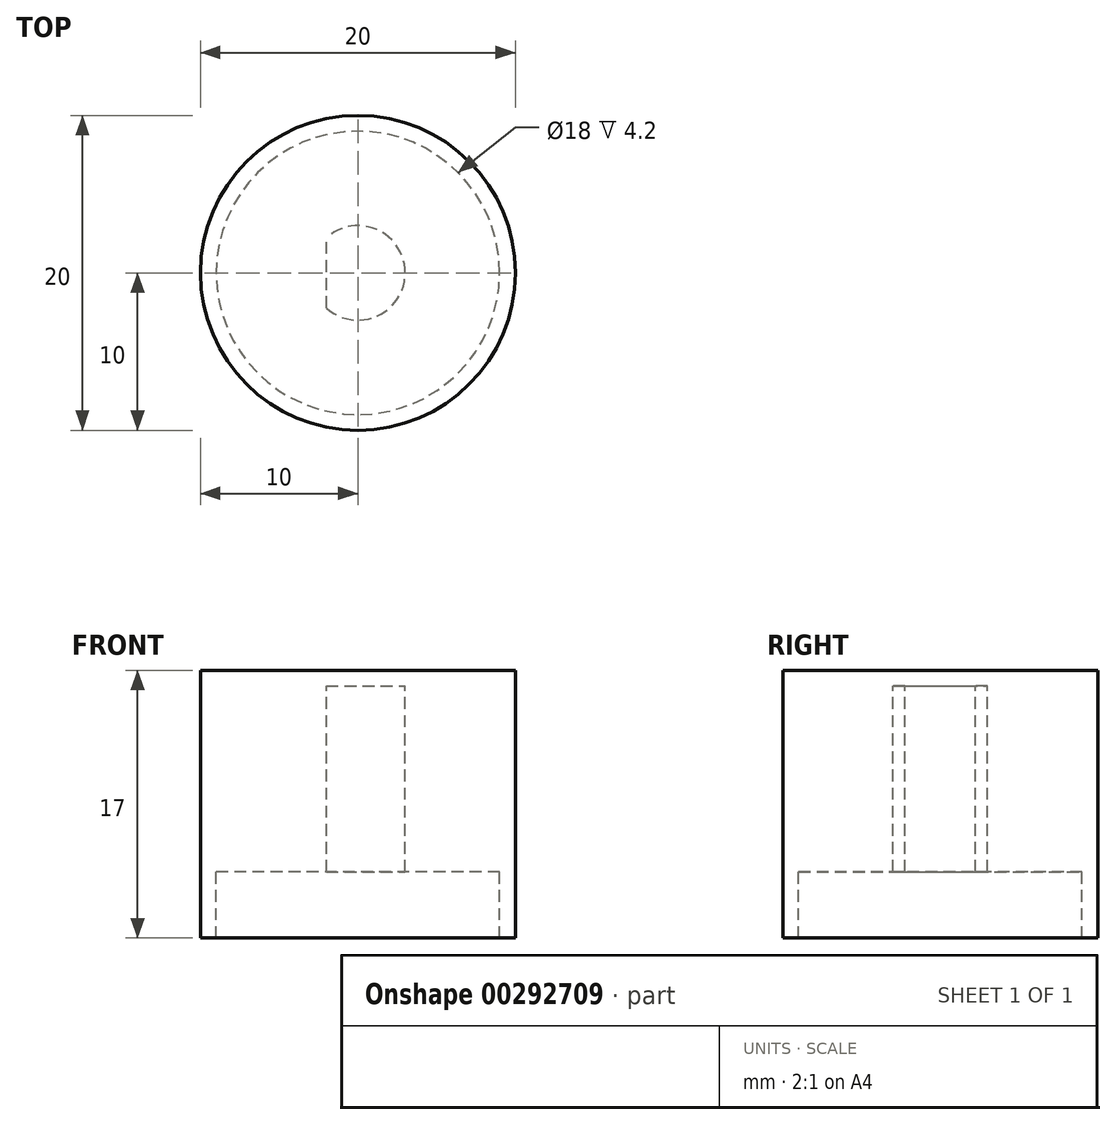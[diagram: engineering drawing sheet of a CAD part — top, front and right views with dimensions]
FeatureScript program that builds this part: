
annotation { "Feature Type Name" : "Feature", "Feature Type Description" : "" }
export const myFeature = defineFeature(function(context is Context, id is Id, definition is map)
    precondition{}
    {
        {
            var Q0;
            Q0=qCreatedBy(makeId("Front.planeOp"),FACE);
            var sketch = newSketch(context, id + "F0", { "sketchPlane" : qUnion([Q0])});
            skLineSegment(sketch, "E0", {"start": v(0, 23.9) * mm, "end": v(0, 0) * mm, "construction": true});
            skLineSegment(sketch, "E1", {"start": v(0, 17) * mm, "end": v(-10, 17) * mm});
            skLineSegment(sketch, "E2", {"start": v(-10, 17) * mm, "end": v(-10, 0) * mm});
            skLineSegment(sketch, "E3", {"start": v(-10, 0) * mm, "end": v(-9, 0) * mm});
            skLineSegment(sketch, "E4", {"start": v(-9, 0) * mm, "end": v(-9, 4.2) * mm});
            skLineSegment(sketch, "E5", {"start": v(-9, 4.2) * mm, "end": v(-3, 4.2) * mm});
            skLineSegment(sketch, "E6", {"start": v(-3, 4.2) * mm, "end": v(-3, 16) * mm});
            skLineSegment(sketch, "E7", {"start": v(-3, 16) * mm, "end": v(0, 16) * mm});
            skLineSegment(sketch, "E8", {"start": v(0, 16) * mm, "end": v(0, 17) * mm});
            skSolve(sketch);
        }
        {
            var Q0;
            Q0 = qSketchRegion(id + "F0", true);
            var Q1;
            Q1=sQuery(id+"F0.wireOp",EDGE,"E0");
            revolve(context, id + "F1", {"entities" : qUnion([Q0]), "axis" : qUnion([Q1]), "revolveType" : RevolveType.FULL});
        }
        {
            var Q0;
            Q0=makeQuery(id+"F1.opRevolve","SWEPT_FACE",FACE,{"disambiguationData":[OSD([sQuery(id+"F0.wireOp",EDGE,"E7")])]});
            var sketch = newSketch(context, id + "F2", { "sketchPlane" : qUnion([Q0])});
            skCircle(sketch, "E9.0", {"center": v(0, 0) * mm, "radius": 3 * mm});
            skLineSegment(sketch, "E10", {"start": v(-2, 2.24) * mm, "end": v(-2, -2.24) * mm});
            skSolve(sketch);
        }
        {
            var Q0;
            {var subQ0=sQuery(id+"F2.wireOp",EDGE,"E10");Q0=makeQuery(id+"F2.imprint","IMPRINT",FACE,{"disambiguationData":[TD([[makeQuery(id+"F2.imprint","IMPRINT",EDGE,{"derivedFrom":subQ0}),-1.0]])]});}
            var Q1;
            Q1=makeQuery(id+"F1.opRevolve","SWEPT_FACE",FACE,{"disambiguationData":[OSD([sQuery(id+"F0.wireOp",EDGE,"E5")])]});
            extrude(context, id + "F3", {"entities" : qUnion([Q0]), "operationType" : NewBodyOperationType.ADD, "endBound" : BoundingType.UP_TO_SURFACE, "endBoundEntityFace" : qUnion([Q1]), "depth" : 25 * mm});
        }
    });
